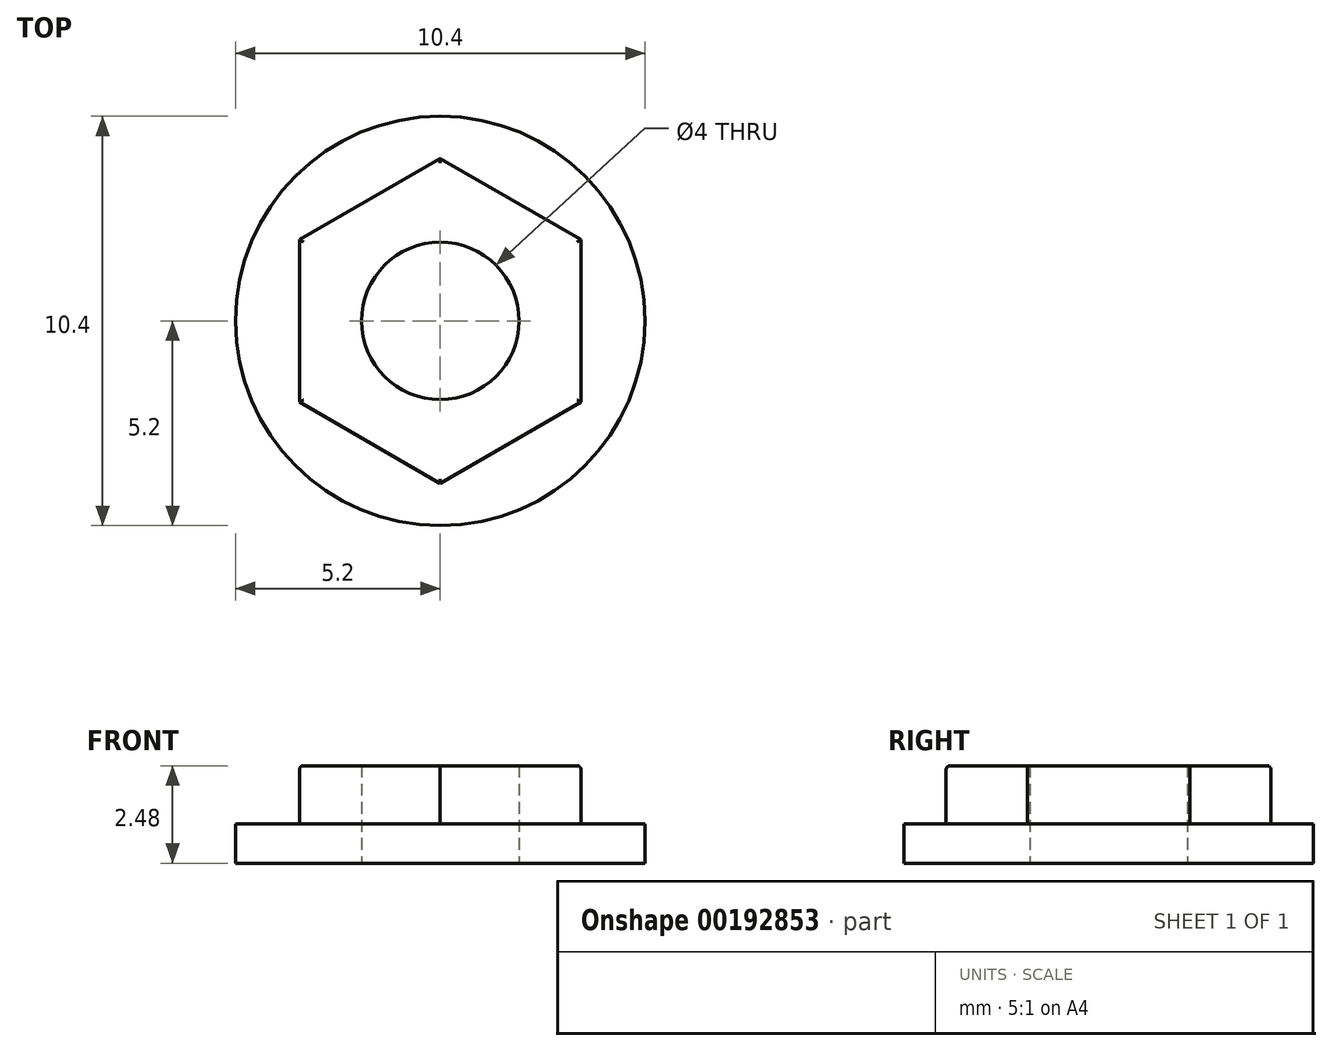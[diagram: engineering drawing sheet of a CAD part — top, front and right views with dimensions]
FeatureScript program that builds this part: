
annotation { "Feature Type Name" : "Feature", "Feature Type Description" : "" }
export const myFeature = defineFeature(function(context is Context, id is Id, definition is map)
    precondition{}
    {
        {
            var Q0;
            Q0=qCreatedBy(makeId("Top.planeOp"),FACE);
            var sketch = newSketch(context, id + "F0", { "sketchPlane" : qUnion([Q0])});
            skCircle(sketch, "E0", {"center": v(0, 0) * mm, "radius": 5.2 * mm});
            skSolve(sketch);
        }
        {
            var Q0;
            Q0 = qSketchRegion(id + "F0", true);
            extrude(context, id + "F1", {"entities" : qUnion([Q0]), "depth" : 1 * mm});
        }
        {
            var Q0;
            Q0=makeQuery(id+"F1.opExtrude","CAP_FACE",FACE,{"disambiguationData":[OSD([sQuery(id+"F0.wireOp",EDGE,"E0")])],"isStart":false});
            var sketch = newSketch(context, id + "F2", { "sketchPlane" : qUnion([Q0])});
            skCircle(sketch, "E1.cCircle", {"center": v(0, 0) * mm, "radius": 3.58 * mm, "construction": true});
            skLineSegment(sketch, "E1.0", {"start": v(3.58, 2.06) * mm, "end": v(3.58, -2.06) * mm});
            skLineSegment(sketch, "E1.1", {"start": v(3.57, -2.06) * mm, "end": v(0, -4.13) * mm});
            skLineSegment(sketch, "E1.2", {"start": v(0, -4.13) * mm, "end": v(-3.57, -2.06) * mm});
            skLineSegment(sketch, "E1.3", {"start": v(-3.57, -2.06) * mm, "end": v(-3.58, 2.06) * mm});
            skLineSegment(sketch, "E1.4", {"start": v(-3.58, 2.06) * mm, "end": v(0, 4.13) * mm});
            skLineSegment(sketch, "E1.5", {"start": v(0, 4.13) * mm, "end": v(3.57, 2.06) * mm});
            skPoint(sketch, "E1.0.midPoint", {"position": v(3.58, 0) * mm});
            skCircle(sketch, "E2", {"center": v(0, 0) * mm, "radius": 2 * mm});
            skSolve(sketch);
        }
        {
            var Q0;
            Q0 = qSketchRegion(id + "F2", true);
            extrude(context, id + "F3", {"entities" : qUnion([Q0]), "operationType" : NewBodyOperationType.ADD, "depth" : 1.48 * mm});
        }
        {
            var Q0;
            Q0=makeQuery(id+"F2.imprint","IMPRINT",FACE,{"disambiguationData":[TD([[makeQuery(id+"F2.imprint","IMPRINT",EDGE,{"derivedFrom":sQuery(id+"F2.wireOp",EDGE,"E2")}),1.0]])]});
            extrude(context, id + "F4", {"entities" : qUnion([Q0]), "operationType" : NewBodyOperationType.REMOVE, "oppositeDirection" : true, "depth" : 25 * mm, "hasSecondDirection" : true, "secondDirectionOppositeDirection" : false, "secondDirectionDepth" : 25 * mm});
        }
        {
            var Q0;
            Q0=makeQuery(id+"F3.opExtrude","CAP_EDGE",EDGE,{"disambiguationData":[OSD([sQuery(id+"F2.wireOp",EDGE,"E1.1")])],"isStart":false});
            var Q1;
            Q1=makeQuery(id+"F3.opExtrude","CAP_EDGE",EDGE,{"disambiguationData":[OSD([sQuery(id+"F2.wireOp",EDGE,"E1.0")])],"isStart":false});
            var Q2;
            Q2=makeQuery(id+"F3.opExtrude","CAP_EDGE",EDGE,{"disambiguationData":[OSD([sQuery(id+"F2.wireOp",EDGE,"E1.2")])],"isStart":false});
            var Q3;
            Q3=makeQuery(id+"F3.opExtrude","CAP_EDGE",EDGE,{"disambiguationData":[OSD([sQuery(id+"F2.wireOp",EDGE,"E1.3")])],"isStart":false});
            var Q4;
            Q4=makeQuery(id+"F3.opExtrude","CAP_EDGE",EDGE,{"disambiguationData":[OSD([sQuery(id+"F2.wireOp",EDGE,"E1.4")])],"isStart":false});
            var Q5;
            Q5=makeQuery(id+"F3.opExtrude","CAP_EDGE",EDGE,{"disambiguationData":[OSD([sQuery(id+"F2.wireOp",EDGE,"E1.5")])],"isStart":false});
            fillet(context, id + "F5", {"entities" : qUnion([Q0, Q1, Q2, Q3, Q4, Q5]), "radius" : 0.1 * mm, "tangentPropagation" : true, "allowEdgeOverflow" : false});
        }
    });
